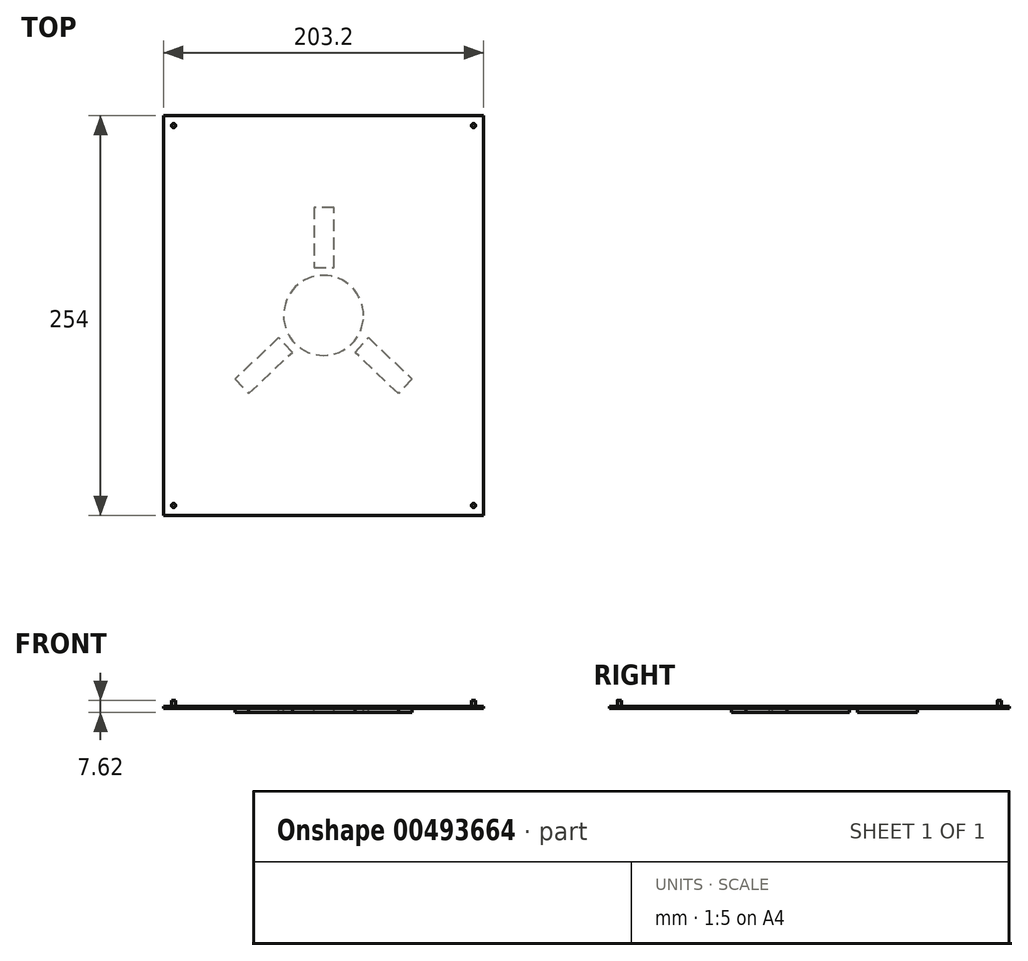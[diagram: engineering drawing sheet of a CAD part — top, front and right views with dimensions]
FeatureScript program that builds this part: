
annotation { "Feature Type Name" : "Feature", "Feature Type Description" : "" }
export const myFeature = defineFeature(function(context is Context, id is Id, definition is map)
    precondition{}
    {
        {
            var Q0;
            Q0=qCreatedBy(makeId("Top.planeOp"),FACE);
            var sketch = newSketch(context, id + "F0", { "sketchPlane" : qUnion([Q0])});
            skLineSegment(sketch, "E0.bottom", {"start": v(101.6, 127) * mm, "end": v(-101.6, 127) * mm});
            skLineSegment(sketch, "E0.top", {"start": v(101.6, -127) * mm, "end": v(-101.6, -127) * mm});
            skLineSegment(sketch, "E0.left", {"start": v(101.6, 127) * mm, "end": v(101.6, -127) * mm});
            skLineSegment(sketch, "E0.right", {"start": v(-101.6, 127) * mm, "end": v(-101.6, -127) * mm});
            skPoint(sketch, "E0.middle", {"position": v(0, 0) * mm});
            skSolve(sketch);
        }
        {
            var Q0;
            Q0=makeQuery(id+"F0.imprint","IMPRINT",FACE,{"disambiguationData":[TD([[makeQuery(id+"F0.imprint","IMPRINT",EDGE,{"derivedFrom":sQuery(id+"F0.wireOp",EDGE,"E0.bottom")}),1.0]])]});
            extrude(context, id + "F1", {"entities" : qUnion([Q0]), "depth" : 1.27 * mm, "offsetDistance" : 25.4 * mm});
        }
        {
            var Q0;
            Q0=makeQuery(id+"F1.opExtrude","CAP_FACE",FACE,{"disambiguationData":[OSD([sQuery(id+"F0.wireOp",EDGE,"E0.bottom"),sQuery(id+"F0.wireOp",EDGE,"E0.top"),sQuery(id+"F0.wireOp",EDGE,"E0.left"),sQuery(id+"F0.wireOp",EDGE,"E0.right")])],"isStart":false});
            var sketch = newSketch(context, id + "F2", { "sketchPlane" : qUnion([Q0])});
            skCircle(sketch, "E1", {"center": v(-95.25, 120.65) * mm, "radius": 1.27 * mm});
            skCircle(sketch, "E2", {"center": v(95.25, 120.65) * mm, "radius": 1.27 * mm});
            skCircle(sketch, "E3", {"center": v(95.25, -120.65) * mm, "radius": 1.27 * mm});
            skCircle(sketch, "E4", {"center": v(-95.25, -120.65) * mm, "radius": 1.27 * mm});
            skSolve(sketch);
        }
        {
            var Q0;
            Q0=makeQuery(id+"F2.imprint","IMPRINT",FACE,{"disambiguationData":[TD([[makeQuery(id+"F2.imprint","IMPRINT",EDGE,{"derivedFrom":sQuery(id+"F2.wireOp",EDGE,"E1")}),1.0]])]});
            var Q1;
            Q1=makeQuery(id+"F2.imprint","IMPRINT",FACE,{"disambiguationData":[TD([[makeQuery(id+"F2.imprint","IMPRINT",EDGE,{"derivedFrom":sQuery(id+"F2.wireOp",EDGE,"E2")}),1.0]])]});
            var Q2;
            Q2=makeQuery(id+"F2.imprint","IMPRINT",FACE,{"disambiguationData":[TD([[makeQuery(id+"F2.imprint","IMPRINT",EDGE,{"derivedFrom":sQuery(id+"F2.wireOp",EDGE,"E3")}),1.0]])]});
            var Q3;
            Q3=makeQuery(id+"F2.imprint","IMPRINT",FACE,{"disambiguationData":[TD([[makeQuery(id+"F2.imprint","IMPRINT",EDGE,{"derivedFrom":sQuery(id+"F2.wireOp",EDGE,"E4")}),1.0]])]});
            extrude(context, id + "F3", {"entities" : qUnion([Q0, Q1, Q2, Q3]), "operationType" : NewBodyOperationType.ADD, "depth" : 3.8 * mm, "offsetDistance" : 25.4 * mm});
        }
        {
            var Q0;
            Q0=makeQuery(id+"F1.opExtrude","CAP_FACE",FACE,{"disambiguationData":[OSD([sQuery(id+"F0.wireOp",EDGE,"E0.bottom"),sQuery(id+"F0.wireOp",EDGE,"E0.top"),sQuery(id+"F0.wireOp",EDGE,"E0.left"),sQuery(id+"F0.wireOp",EDGE,"E0.right")])],"isStart":true});
            var sketch = newSketch(context, id + "F4", { "sketchPlane" : qUnion([Q0])});
            skCircle(sketch, "E5", {"center": v(0, 0) * mm, "radius": 25.4 * mm});
            skLineSegment(sketch, "E6", {"start": v(-28.57, 14.16) * mm, "end": v(-56.23, 40.37) * mm});
            skLineSegment(sketch, "E7", {"start": v(-56.23, 40.37) * mm, "end": v(-47.5, 49.59) * mm});
            skLineSegment(sketch, "E8", {"start": v(-47.5, 49.59) * mm, "end": v(-19.84, 23.38) * mm});
            skLineSegment(sketch, "E9", {"start": v(-19.84, 23.38) * mm, "end": v(-28.57, 14.16) * mm});
            skLineSegment(sketch, "E10", {"start": v(0, 83.38) * mm, "end": v(0, -72.88) * mm, "construction": true});
            skLineSegment(sketch, "E11.MirrorCS", {"start": v(47.5, 49.59) * mm, "end": v(19.84, 23.38) * mm});
            skLineSegment(sketch, "E12.MirrorCS", {"start": v(56.23, 40.37) * mm, "end": v(47.5, 49.59) * mm});
            skLineSegment(sketch, "E13.MirrorCS", {"start": v(28.57, 14.16) * mm, "end": v(56.23, 40.37) * mm});
            skLineSegment(sketch, "E14.MirrorCS", {"start": v(19.84, 23.38) * mm, "end": v(28.57, 14.16) * mm});
            skLineSegment(sketch, "E15", {"start": v(-6.05, -30.48) * mm, "end": v(6.65, -30.48) * mm});
            skLineSegment(sketch, "E16", {"start": v(6.65, -30.48) * mm, "end": v(6.65, -68.58) * mm});
            skLineSegment(sketch, "E17", {"start": v(6.65, -68.58) * mm, "end": v(-6.05, -68.58) * mm});
            skLineSegment(sketch, "E18", {"start": v(-6.05, -68.58) * mm, "end": v(-6.05, -30.48) * mm});
            skSolve(sketch);
        }
        {
            var Q0;
            Q0=makeQuery(id+"F4.imprint","IMPRINT",FACE,{"disambiguationData":[TD([[makeQuery(id+"F4.imprint","IMPRINT",EDGE,{"derivedFrom":sQuery(id+"F4.wireOp",EDGE,"E6")}),-1.0]])]});
            var Q1;
            Q1=makeQuery(id+"F4.imprint","IMPRINT",FACE,{"disambiguationData":[TD([[makeQuery(id+"F4.imprint","IMPRINT",EDGE,{"derivedFrom":sQuery(id+"F4.wireOp",EDGE,"E5")}),1.0]])]});
            var Q2;
            Q2=makeQuery(id+"F4.imprint","IMPRINT",FACE,{"disambiguationData":[TD([[makeQuery(id+"F4.imprint","IMPRINT",EDGE,{"derivedFrom":sQuery(id+"F4.wireOp",EDGE,"E11.MirrorCS")}),1.0]])]});
            var Q3;
            Q3=makeQuery(id+"F4.imprint","IMPRINT",FACE,{"disambiguationData":[TD([[makeQuery(id+"F4.imprint","IMPRINT",EDGE,{"derivedFrom":sQuery(id+"F4.wireOp",EDGE,"E15")}),-1.0]])]});
            extrude(context, id + "F5", {"entities" : qUnion([Q0, Q1, Q2, Q3]), "operationType" : NewBodyOperationType.ADD, "depth" : 2.54 * mm, "offsetDistance" : 25.4 * mm});
        }
    });
